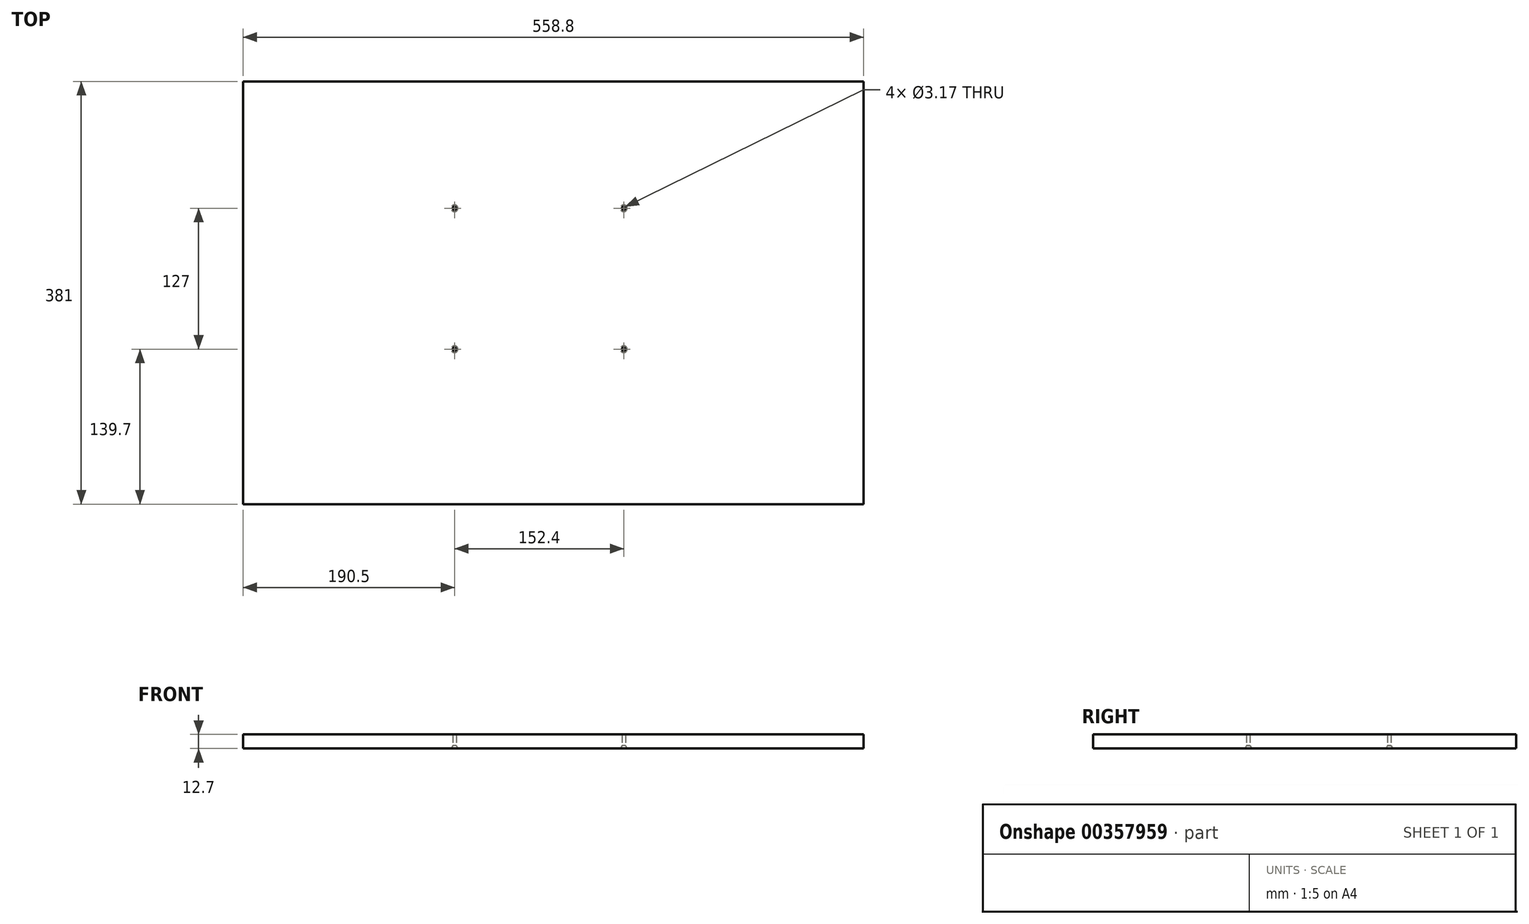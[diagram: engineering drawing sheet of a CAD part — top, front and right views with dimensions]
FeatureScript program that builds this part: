
annotation { "Feature Type Name" : "Feature", "Feature Type Description" : "" }
export const myFeature = defineFeature(function(context is Context, id is Id, definition is map)
    precondition{}
    {
        {
            var Q0;
            Q0=qCreatedBy(makeId("Top.planeOp"),FACE);
            var sketch = newSketch(context, id + "F0", { "sketchPlane" : qUnion([Q0])});
            skLineSegment(sketch, "E0.bottom", {"start": v(279.4, -190.5) * mm, "end": v(-279.4, -190.5) * mm});
            skLineSegment(sketch, "E0.top", {"start": v(279.4, 190.5) * mm, "end": v(-279.4, 190.5) * mm});
            skLineSegment(sketch, "E0.left", {"start": v(279.4, -190.5) * mm, "end": v(279.4, 190.5) * mm});
            skLineSegment(sketch, "E0.right", {"start": v(-279.4, -190.5) * mm, "end": v(-279.4, 190.5) * mm});
            skPoint(sketch, "E0.middle", {"position": v(0, 0) * mm});
            skCircle(sketch, "E1", {"center": v(-88.9, 76.2) * mm, "radius": 1.59 * mm});
            skCircle(sketch, "E2.0.1.0", {"center": v(-88.9, -50.8) * mm, "radius": 1.59 * mm});
            skCircle(sketch, "E2.1.0.0", {"center": v(63.5, 76.2) * mm, "radius": 1.59 * mm});
            skCircle(sketch, "E2.1.1.0", {"center": v(63.5, -50.8) * mm, "radius": 1.59 * mm});
            skLineSegment(sketch, "E2.direction1", {"start": v(-88.9, 76.2) * mm, "end": v(63.5, 76.2) * mm, "construction": true});
            skLineSegment(sketch, "E2.direction2", {"start": v(-88.9, 76.2) * mm, "end": v(-88.9, -50.8) * mm, "construction": true});
            skSolve(sketch);
        }
        {
            var Q0;
            Q0=makeQuery(id+"F0.imprint","IMPRINT",FACE,{"disambiguationData":[TD([[makeQuery(id+"F0.imprint","IMPRINT",EDGE,{"derivedFrom":sQuery(id+"F0.wireOp",EDGE,"E0.bottom")}),-1.0]])]});
            extrude(context, id + "F1", {"entities" : qUnion([Q0]), "depth" : 12.7 * mm});
        }
        {
            var Q0;
            Q0=makeQuery(id+"F1.opExtrude","CAP_EDGE",EDGE,{"disambiguationData":[OSD([sQuery(id+"F0.wireOp",EDGE,"E2.0.1.0")])],"isStart":true});
            var Q1;
            Q1=makeQuery(id+"F1.opExtrude","CAP_EDGE",EDGE,{"disambiguationData":[OSD([sQuery(id+"F0.wireOp",EDGE,"E2.1.1.0")])],"isStart":true});
            var Q2;
            Q2=makeQuery(id+"F1.opExtrude","CAP_EDGE",EDGE,{"disambiguationData":[OSD([sQuery(id+"F0.wireOp",EDGE,"E1")])],"isStart":true});
            var Q3;
            Q3=makeQuery(id+"F1.opExtrude","CAP_EDGE",EDGE,{"disambiguationData":[OSD([sQuery(id+"F0.wireOp",EDGE,"E2.1.0.0")])],"isStart":true});
            chamfer(context, id + "F2", {"entities" : qUnion([Q0, Q1, Q2, Q3]), "chamferType" : ChamferType.OFFSET_ANGLE, "width" : 2.54 * mm, "oppositeDirection" : true, "angle" : 30 * degree, "tangentPropagation" : true});
        }
    });
